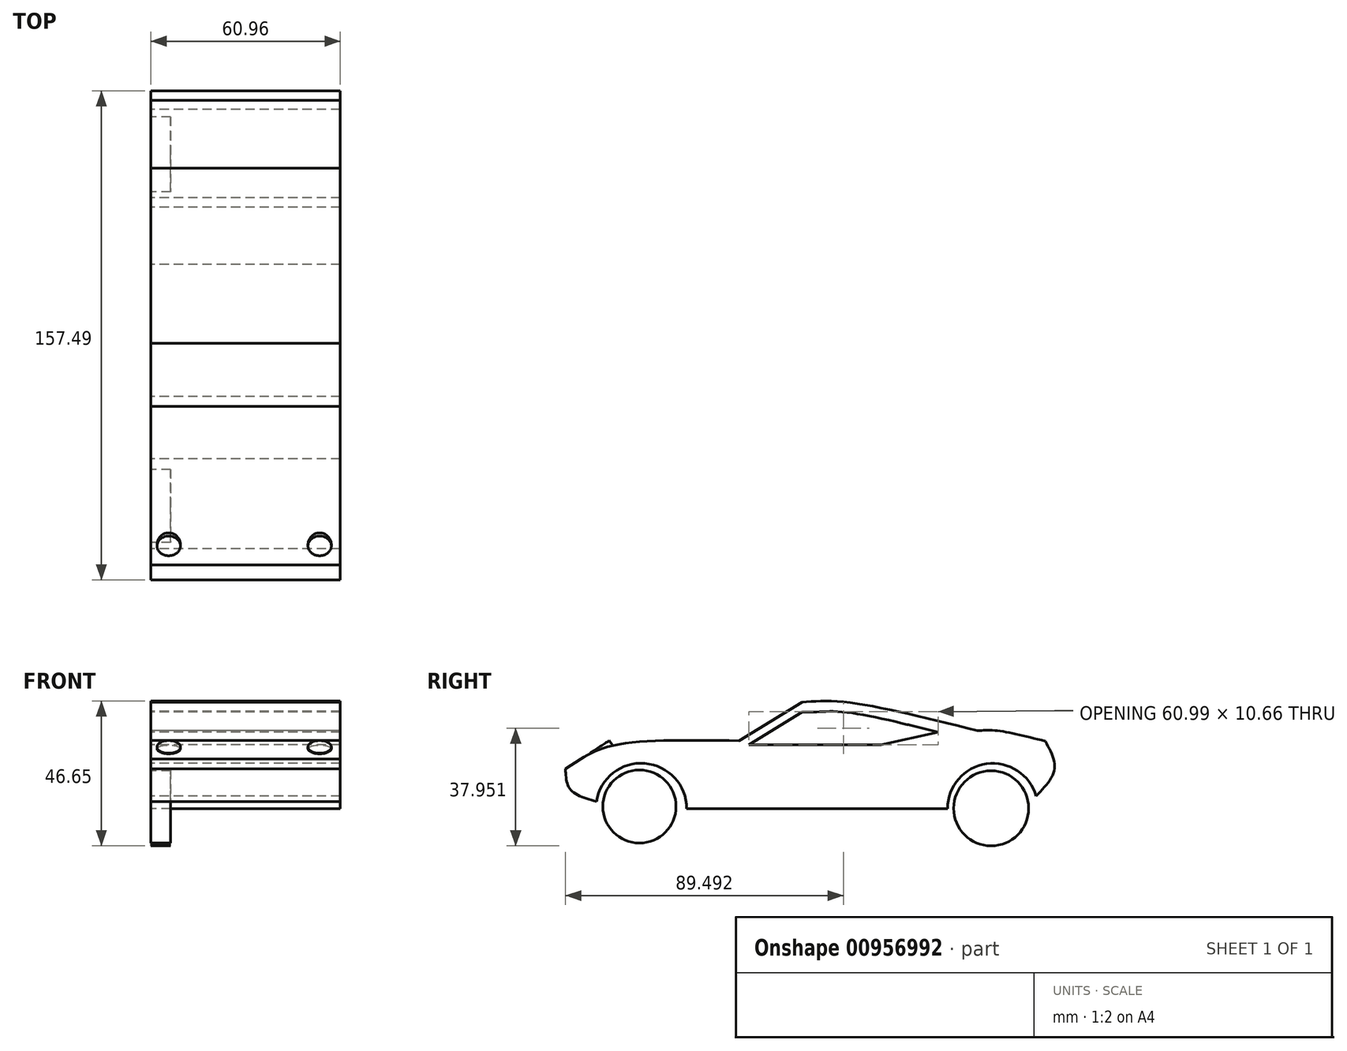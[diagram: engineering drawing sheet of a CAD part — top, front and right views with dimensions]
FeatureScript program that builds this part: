
annotation { "Feature Type Name" : "Feature", "Feature Type Description" : "" }
export const myFeature = defineFeature(function(context is Context, id is Id, definition is map)
    precondition{}
    {
        {
            var Q0;
            Q0=qCreatedBy(makeId("Right.planeOp"),FACE);
            var sketch = newSketch(context, id + "F0", { "sketchPlane" : qUnion([Q0])});
            skPoint(sketch, "E0.0.internal.orphan", {"position": v(-64.14, 0) * mm});
            skFitSpline(sketch, "E1", {"points": [v(-64.14, 0) * mm, v(-53.83, 4.4) * mm, v(-13.18, 5.91) * mm], "startDerivative": vector(24.44, 14.58) * mm, "endDerivative": vector(72.5, -1.12) * mm});
            skLineSegment(sketch, "E2", {"start": v(-13.18, 5.91) * mm, "end": v(7.15, 18.35) * mm});
            skFitSpline(sketch, "E3", {"points": [v(7.15, 18.35) * mm, v(21.12, 18.35) * mm, v(63.61, 9.15) * mm], "startDerivative": vector(33.57, 2.6) * mm, "endDerivative": vector(75.5, -19.01) * mm});
            skFitSpline(sketch, "E4", {"points": [v(63.61, 9.15) * mm, v(69.99, 9.15) * mm, v(85.46, 5.79) * mm], "startDerivative": vector(14.7, 1.07) * mm, "endDerivative": vector(28.01, -7.17) * mm});
            skFitSpline(sketch, "E5", {"points": [v(-64.14, 0) * mm, v(-69.01, -3.16) * mm], "startDerivative": vector(-4.87, -3.16) * mm, "endDerivative": vector(-4.87, -3.16) * mm});
            skLineSegment(sketch, "E6", {"start": v(-30, -15.92) * mm, "end": v(54, -15.92) * mm});
            skArc(sketch, "E7", {"start": v(-30, -15.92) * mm, "mid": v(-43.48, -1.36) * mm, "end": v(-59.03, -13.69) * mm});
            skArc(sketch, "E8", {"start": v(82.53, -11.91) * mm, "mid": v(66.52, -1.52) * mm, "end": v(54, -15.92) * mm});
            skPoint(sketch, "E9", {"position": v(-59.03, -13.69) * mm});
            skPoint(sketch, "E10", {"position": v(-58.64, -13.74) * mm});
            skPoint(sketch, "E11", {"position": v(-30, -15.92) * mm});
            skPoint(sketch, "E12", {"position": v(-29.87, -15.85) * mm});
            skPoint(sketch, "E13", {"position": v(54, -15.92) * mm});
            skPoint(sketch, "E14", {"position": v(54.32, -15.55) * mm});
            skPoint(sketch, "E15", {"position": v(82.53, -11.91) * mm});
            skPoint(sketch, "E16", {"position": v(82.48, -11.93) * mm});
            skFitSpline(sketch, "E17", {"points": [v(-69.01, -3.16) * mm, v(-67.39, -9.81) * mm, v(-58.64, -13.74) * mm], "startDerivative": vector(0.66, -16.2) * mm, "endDerivative": vector(19.56, -5.27) * mm});
            skFitSpline(sketch, "E18", {"points": [v(85.46, 5.79) * mm, v(88.42, -3.16) * mm, v(82.53, -11.91) * mm], "startDerivative": vector(10.33, -18.75) * mm, "endDerivative": vector(-15.96, -16.67) * mm});
            skLineSegment(sketch, "E19", {"start": v(-10.02, 4.68) * mm, "end": v(7.15, 15.18) * mm});
            skFitSpline(sketch, "E20", {"points": [v(7.15, 15.18) * mm, v(11.2, 15.18) * mm, v(20.47, 15.18) * mm, v(50.98, 8.63) * mm], "startDerivative": vector(20.06, -0.46) * mm, "endDerivative": vector(65.78, -16.75) * mm});
            skLineSegment(sketch, "E21", {"start": v(-10.02, 4.68) * mm, "end": v(32.55, 4.68) * mm});
            skLineSegment(sketch, "E22", {"start": v(32.55, 4.68) * mm, "end": v(50.98, 8.63) * mm});
            skLineSegment(sketch, "E23", {"start": v(32.55, 4.68) * mm, "end": v(39.47, 11.56) * mm});
            skFitSpline(sketch, "E24", {"points": [v(-26.94, 0) * mm, v(-24.83, -6.59) * mm, v(-20.6, -11.42) * mm, v(0, -13.2) * mm, v(0, -13.2) * mm], "startDerivative": vector(8.42, -25.28) * mm, "endDerivative": vector(-0.3, 0.44) * mm});
            skLineSegment(sketch, "E25", {"start": v(-24.83, -6.59) * mm, "end": v(-13.62, -6.59) * mm});
            skLineSegment(sketch, "E26", {"start": v(-20.37, -11.4) * mm, "end": v(-3.66, -11.09) * mm});
            skLineSegment(sketch, "E27", {"start": v(-10.02, 4.68) * mm, "end": v(-3.66, -5.7) * mm});
            skPoint(sketch, "E28", {"position": v(31.36, -5.7) * mm});
            skPoint(sketch, "E29", {"position": v(113.62, -4.34) * mm});
            skFitSpline(sketch, "E30", {"points": [v(-3.66, -5.7) * mm, v(0, -8.6) * mm, v(21.28, -11.09) * mm, v(25.5, -8) * mm, v(32.55, 4.68) * mm], "startDerivative": vector(12.88, -17.95) * mm, "endDerivative": vector(26.78, 49.9) * mm});
            skSolve(sketch);
        }
        {
            var Q0;
            Q0=makeQuery(id+"F0.imprint","IMPRINT",FACE,{"disambiguationData":[TD([[makeQuery(id+"F0.imprint","IMPRINT",EDGE,{"derivedFrom":sQuery(id+"F0.wireOp",EDGE,"E1")}),-1.0]])]});
            var Q1;
            Q1=makeQuery(id+"F0.imprint","IMPRINT",FACE,{"disambiguationData":[TD([[makeQuery(id+"F0.imprint","IMPRINT",EDGE,{"derivedFrom":sQuery(id+"F0.wireOp",EDGE,"E21")}),-1.0]])]});
            extrude(context, id + "F1", {"entities" : qUnion([Q0, Q1]), "depth" : 60.96 * mm, "offsetDistance" : 25.4 * mm});
        }
        {
            var Q0;
            Q0=makeQuery(id+"F1.opExtrude","SWEPT_FACE",FACE,{"disambiguationData":[OSD([sQuery(id+"F0.wireOp",EDGE,"E5")])]});
            var sketch = newSketch(context, id + "F2", { "sketchPlane" : qUnion([Q0])});
            skPoint(sketch, "E31.left.start.orphan", {"position": v(0, 16.76) * mm});
            skPoint(sketch, "E32.start.orphan", {"position": v(0, 7.1) * mm});
            skPoint(sketch, "E33.end.orphan", {"position": v(22.53, 7.1) * mm});
            skPoint(sketch, "E34.end.orphan", {"position": v(2.57, 7.1) * mm});
            skPoint(sketch, "E35.end.orphan", {"position": v(58.72, 7.1) * mm});
            skPoint(sketch, "E36.start.orphan", {"position": v(2.57, 16.76) * mm});
            skPoint(sketch, "E37", {"position": v(43.78, 0) * mm});
            skPoint(sketch, "E38", {"position": v(65.88, 21.36) * mm});
            skPoint(sketch, "E39", {"position": v(8.4, 21.36) * mm});
            skPoint(sketch, "E40", {"position": v(-12.1, 0) * mm});
            skCircle(sketch, "E41", {"center": v(5.69, -46.58) * mm, "radius": 3.77 * mm});
            skCircle(sketch, "E42", {"center": v(54.3, -46.58) * mm, "radius": 3.77 * mm});
            skSolve(sketch);
        }
        {
            var Q0;
            Q0 = qSketchRegion(id + "F2", true);
            extrude(context, id + "F3", {"entities" : qUnion([Q0]), "operationType" : NewBodyOperationType.ADD, "oppositeDirection" : true, "depth" : 5.08 * mm, "offsetDistance" : 25.4 * mm});
        }
        {
            var Q0;
            Q0=qCreatedBy(makeId("Right.planeOp"),FACE);
            var sketch = newSketch(context, id + "F4", { "sketchPlane" : qUnion([Q0])});
            skCircle(sketch, "E43", {"center": v(-45.2, -15.25) * mm, "radius": 11.78 * mm});
            skCircle(sketch, "E44", {"center": v(68.03, -15.85) * mm, "radius": 12.09 * mm});
            skSolve(sketch);
        }
        {
            var Q0;
            Q0=makeQuery(id+"F4.imprint","IMPRINT",FACE,{"disambiguationData":[TD([[makeQuery(id+"F4.imprint","IMPRINT",EDGE,{"derivedFrom":sQuery(id+"F4.wireOp",EDGE,"E44")}),1.0]])]});
            var Q1;
            Q1=makeQuery(id+"F4.imprint","IMPRINT",FACE,{"disambiguationData":[TD([[makeQuery(id+"F4.imprint","IMPRINT",EDGE,{"derivedFrom":sQuery(id+"F4.wireOp",EDGE,"E43")}),1.0]])]});
            extrude(context, id + "F5", {"entities" : qUnion([Q0, Q1]), "depth" : 6.35 * mm, "offsetDistance" : 25.4 * mm});
        }
    });
